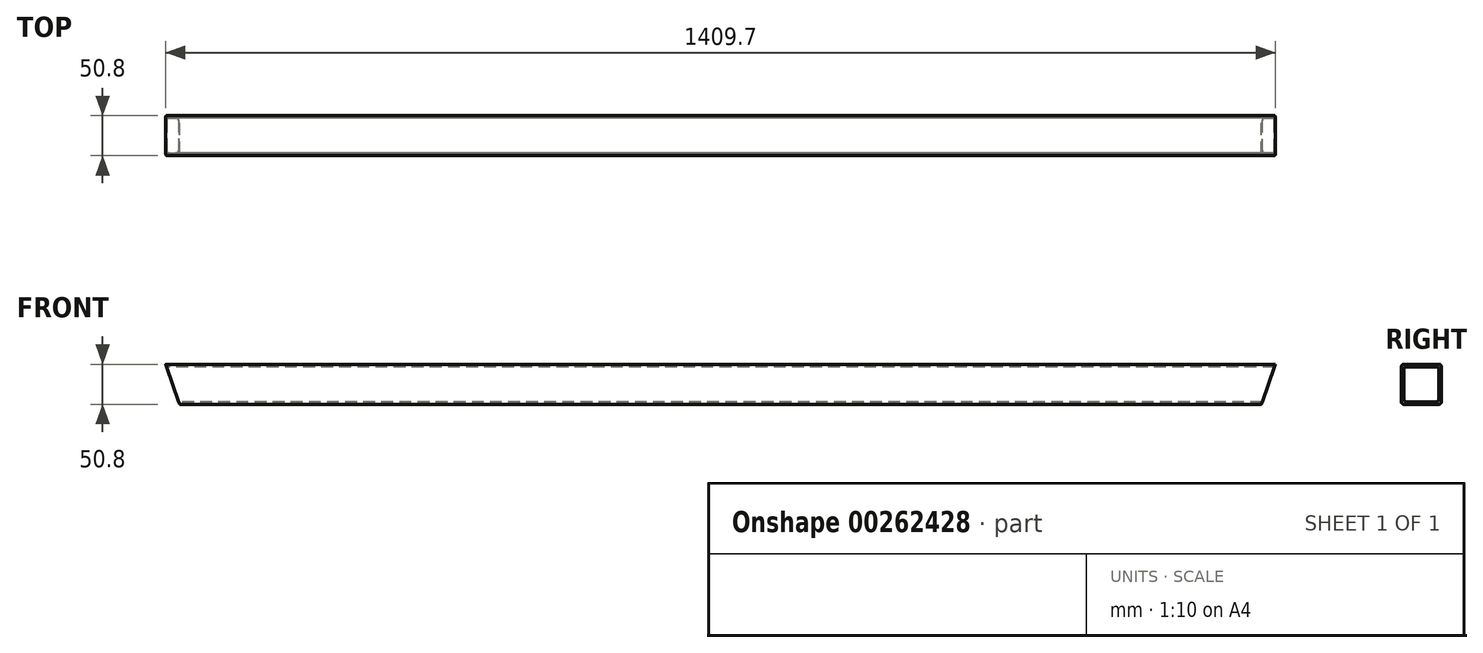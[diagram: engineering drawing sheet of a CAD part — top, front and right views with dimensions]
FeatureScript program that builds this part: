
annotation { "Feature Type Name" : "Feature", "Feature Type Description" : "" }
export const myFeature = defineFeature(function(context is Context, id is Id, definition is map)
    precondition{}
    {
        {
            var Q0;
            Q0=qCreatedBy(makeId("Right.planeOp"),FACE);
            var sketch = newSketch(context, id + "F0", { "sketchPlane" : qUnion([Q0])});
            skLineSegment(sketch, "E0.bottom", {"start": v(22.23, 25.4) * mm, "end": v(-22.23, 25.4) * mm});
            skLineSegment(sketch, "E0.top", {"start": v(22.23, -25.4) * mm, "end": v(-22.23, -25.4) * mm});
            skLineSegment(sketch, "E0.left", {"start": v(25.4, 22.23) * mm, "end": v(25.4, -22.23) * mm});
            skLineSegment(sketch, "E0.right", {"start": v(-25.4, 22.23) * mm, "end": v(-25.4, -22.23) * mm});
            skPoint(sketch, "E0.middle", {"position": v(0, 0) * mm});
            skLineSegment(sketch, "E1.bottom", {"start": v(19.05, 22.23) * mm, "end": v(-19.05, 22.23) * mm});
            skLineSegment(sketch, "E1.top", {"start": v(19.05, -22.22) * mm, "end": v(-19.05, -22.22) * mm});
            skLineSegment(sketch, "E1.left", {"start": v(22.23, 19.05) * mm, "end": v(22.23, -19.05) * mm});
            skLineSegment(sketch, "E1.right", {"start": v(-22.23, 19.05) * mm, "end": v(-22.23, -19.05) * mm});
            skPoint(sketch, "E2.visualSharp", {"position": v(-22.23, 22.23) * mm});
            skArc(sketch, "E2.filletArc", {"start": v(-19.05, 22.23) * mm, "mid": v(-21.3, 21.3) * mm, "end": v(-22.23, 19.05) * mm});
            skPoint(sketch, "E3.visualSharp", {"position": v(-25.4, 25.4) * mm});
            skArc(sketch, "E3.filletArc", {"start": v(-22.23, 25.4) * mm, "mid": v(-24.47, 24.47) * mm, "end": v(-25.4, 22.23) * mm});
            skPoint(sketch, "E4.visualSharp", {"position": v(-22.23, -22.22) * mm});
            skArc(sketch, "E4.filletArc", {"start": v(-22.23, -19.05) * mm, "mid": v(-21.3, -21.3) * mm, "end": v(-19.05, -22.23) * mm});
            skPoint(sketch, "E5.visualSharp", {"position": v(-25.4, -25.4) * mm});
            skArc(sketch, "E5.filletArc", {"start": v(-25.4, -22.23) * mm, "mid": v(-24.47, -24.47) * mm, "end": v(-22.23, -25.4) * mm});
            skPoint(sketch, "E6.visualSharp", {"position": v(22.23, 22.23) * mm});
            skArc(sketch, "E6.filletArc", {"start": v(22.23, 19.05) * mm, "mid": v(21.3, 21.3) * mm, "end": v(19.05, 22.23) * mm});
            skPoint(sketch, "E7.visualSharp", {"position": v(25.4, 25.4) * mm});
            skArc(sketch, "E7.filletArc", {"start": v(25.4, 22.23) * mm, "mid": v(24.47, 24.47) * mm, "end": v(22.23, 25.4) * mm});
            skPoint(sketch, "E8.visualSharp", {"position": v(22.23, -22.22) * mm});
            skArc(sketch, "E8.filletArc", {"start": v(19.05, -22.22) * mm, "mid": v(21.3, -21.3) * mm, "end": v(22.23, -19.05) * mm});
            skPoint(sketch, "E9.visualSharp", {"position": v(25.4, -25.4) * mm});
            skArc(sketch, "E9.filletArc", {"start": v(22.23, -25.4) * mm, "mid": v(24.47, -24.47) * mm, "end": v(25.4, -22.23) * mm});
            skSolve(sketch);
        }
        {
            var Q0;
            Q0 = qSketchRegion(id + "F0", true);
            extrude(context, id + "F1", {"entities" : qUnion([Q0]), "depth" : 1409.7 * mm});
        }
        {
            var Q0;
            Q0=qCreatedBy(makeId("Front.planeOp"),FACE);
            var sketch = newSketch(context, id + "F2", { "sketchPlane" : qUnion([Q0])});
            skLineSegment(sketch, "E10.top", {"start": v(17.82, -25.4) * mm, "end": v(0, -25.4) * mm});
            skLineSegment(sketch, "E10.right", {"start": v(0, 25.4) * mm, "end": v(0, -25.4) * mm});
            skPoint(sketch, "E10.middle", {"position": v(8.9, 0) * mm});
            skLineSegment(sketch, "E11.top", {"start": v(1409.7, -25.4) * mm, "end": v(1391.88, -25.4) * mm});
            skLineSegment(sketch, "E11.left", {"start": v(1409.7, 25.4) * mm, "end": v(1409.7, -25.4) * mm});
            skPoint(sketch, "E11.middle", {"position": v(1400.8, 0) * mm});
            skLineSegment(sketch, "E12", {"start": v(0, 25.4) * mm, "end": v(17.82, -25.4) * mm});
            skPoint(sketch, "E10.bottom.start.orphan", {"position": v(17.82, 25.4) * mm});
            skLineSegment(sketch, "E13", {"start": v(1391.88, -25.4) * mm, "end": v(1409.7, 25.4) * mm});
            skPoint(sketch, "E11.bottom.end.orphan", {"position": v(1391.88, 25.4) * mm});
            skSolve(sketch);
        }
        {
            var Q0;
            Q0 = qSketchRegion(id + "F2", true);
            extrude(context, id + "F3", {"entities" : qUnion([Q0]), "operationType" : NewBodyOperationType.REMOVE, "depth" : 25.4 * mm, "hasSecondDirection" : true, "secondDirectionOppositeDirection" : true, "secondDirectionDepth" : 25.4 * mm});
        }
    });
